# Revit family: R859KX026_027
name_source: partatom
category: Generic Models
revit_build: Autodesk Revit 2018 (Build: 20170223_1515(x64)
units: mm (PartAtom-declared; Revit-internal decimal feet)

## family parameters
Always vertical = Yes
Can host rebar = No
Cut with Voids When Loaded = No
Part Type = Normal
Room Calculation Point = No
Round Connector Dimension = Use Diameter
Shared = No
Work Plane-Based = No

## types (2) — shared parameters
Description = Ball valve, with female-tail piece male threaded connections.
Manufacturer = Giacomini S.p.A.
Material = Giacomini Steel Red
URL = https://www.giacomini.com

## per-type parameters (varying)
| type | DN | Model |
| R859KX026_3/4" F X 1" M | 19 mm | R859KX026 |
| R859KX027_1" M X 1" F | 25 mm  [stored 0.082021 ft] | R859KX027 |

note: [stored X ft] marks values corroborated as IEEE doubles in the binary element streams (Revit-internal decimal feet)

## geometry (parser evidence)
native form markers: Sweep x5
no freeform markers — native parametric forms only
